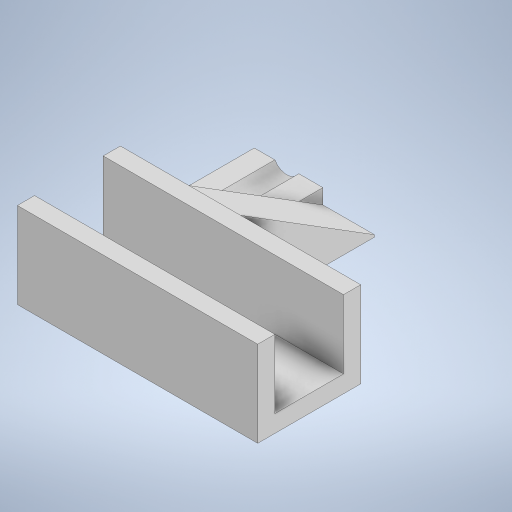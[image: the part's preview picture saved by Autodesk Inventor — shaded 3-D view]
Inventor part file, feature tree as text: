
AUTODESK INVENTOR PART (.ipt)
format: ipt  version: 2024 (Build 280153000, 153)  size: 270,848 bytes
history: native  units: mm
features: extrude x6, sketch x6
ambient origin geometry x8: Origin, YZ Plane, XZ Plane, XY Plane, X Axis, Y Axis, Z Axis, Center Point
bodies: Solid1 (feature_tree)
feature tree (12):
  extrude  "Extrusion1"  Depth=70.0mm
  extrude  "Extrusion2"  Depth=60.0mm
  extrude  "Extrusion3"  Depth=50.0mm
  extrude  "Extrusion4"  Depth=40.0mm
  extrude  "Extrusion5"  Depth=140.0mm TaperAngle=0.0deg
  extrude  "Extrusion6"  Depth=30.0mm TaperAngle=0.0deg
  sketch  "Sketch1"  dims[d0=80.0mm d1=70.0mm]
  sketch  "Sketch2"  dims[d2=30.0mm d3=60.0mm]
  sketch  "Sketch4"  dims[d4=10.0mm d5=0.0mm d6=50.0mm]
  sketch  "Sketch6"  dims[d7=50.0mm d8=40.0mm]
  sketch  "Sketch7"  dims[d9=40.0mm d10=140.0mm d11=0.0mm]
  sketch  "Sketch8"  dims[d12=50.0mm d13=0.0mm d14=30.0mm d15=0.0mm d16=1000.0mm d17=0.0mm d18=10.0mm d19=1000.0mm d20=0.0mm]
